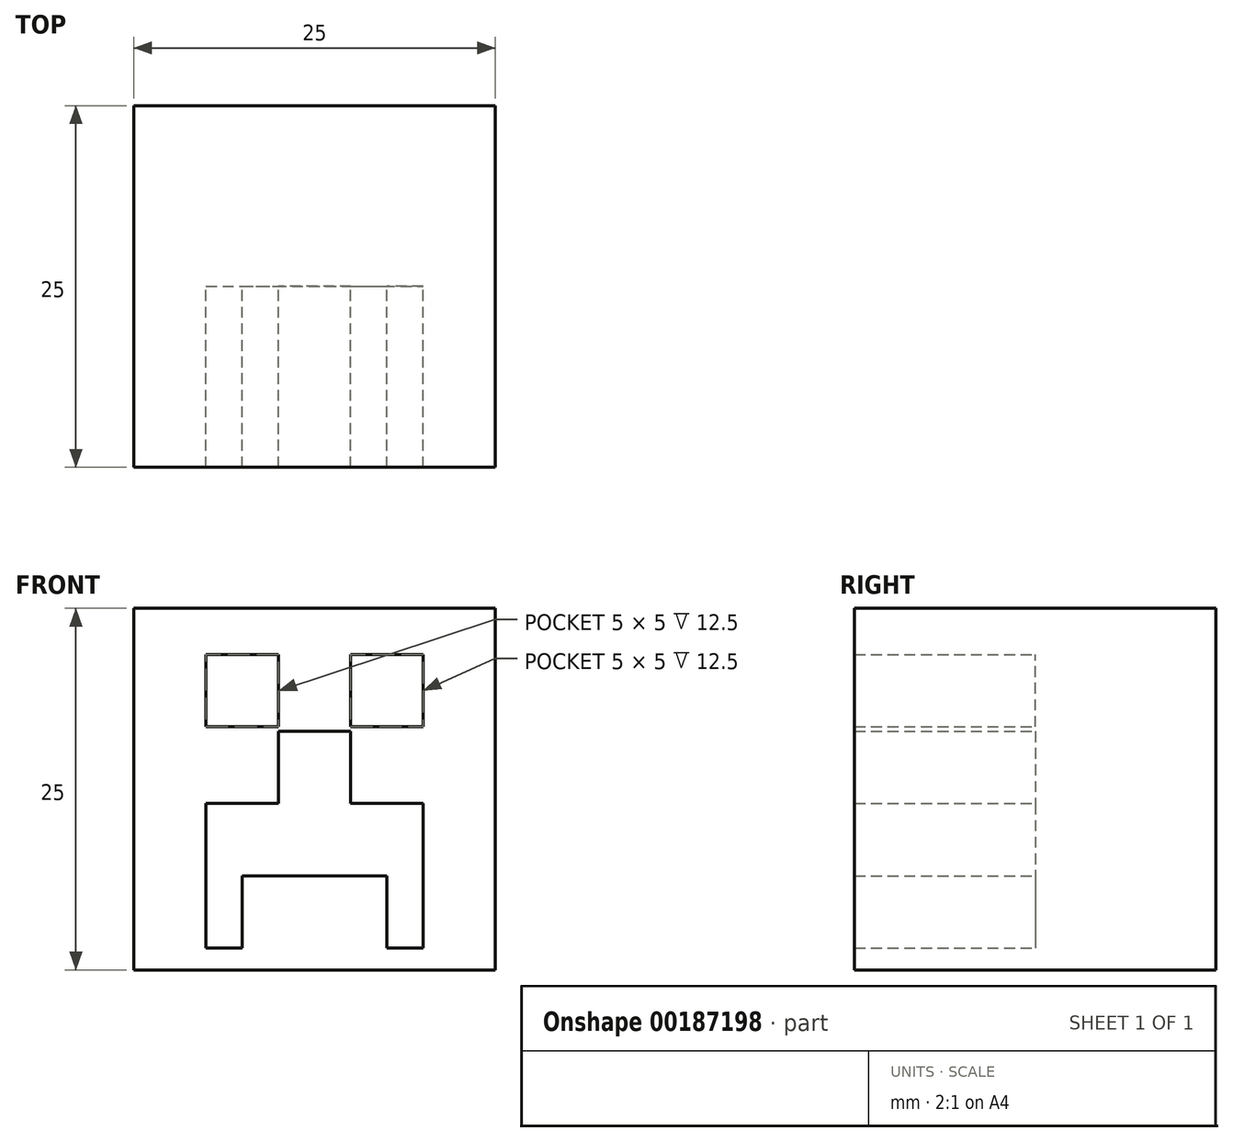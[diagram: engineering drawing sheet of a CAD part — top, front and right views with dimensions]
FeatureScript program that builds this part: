
annotation { "Feature Type Name" : "Feature", "Feature Type Description" : "" }
export const myFeature = defineFeature(function(context is Context, id is Id, definition is map)
    precondition{}
    {
        {
            var Q0;
            Q0=qCreatedBy(makeId("Front.planeOp"),FACE);
            var sketch = newSketch(context, id + "F0", { "sketchPlane" : qUnion([Q0])});
            skLineSegment(sketch, "E0.bottom", {"start": v(0, 0) * mm, "end": v(25, 0) * mm});
            skLineSegment(sketch, "E0.top", {"start": v(0, 25) * mm, "end": v(25, 25) * mm});
            skLineSegment(sketch, "E0.left", {"start": v(0, 0) * mm, "end": v(0, 25) * mm});
            skLineSegment(sketch, "E0.right", {"start": v(25, 0) * mm, "end": v(25, 25) * mm});
            skLineSegment(sketch, "E1.top", {"start": v(5, 21.8) * mm, "end": v(10, 21.8) * mm});
            skLineSegment(sketch, "E1.left", {"start": v(5, 16.8) * mm, "end": v(5, 21.8) * mm});
            skLineSegment(sketch, "E2.top", {"start": v(15, 21.8) * mm, "end": v(20, 21.8) * mm});
            skLineSegment(sketch, "E2.right", {"start": v(20, 16.8) * mm, "end": v(20, 21.8) * mm});
            skLineSegment(sketch, "E3.bottom", {"start": v(15, 16.5) * mm, "end": v(10, 16.5) * mm});
            skLineSegment(sketch, "E3.left", {"start": v(15, 16.5) * mm, "end": v(15, 11.5) * mm});
            skLineSegment(sketch, "E3.right", {"start": v(10, 16.5) * mm, "end": v(10, 11.5) * mm});
            skLineSegment(sketch, "E4.left", {"start": v(5, 11.5) * mm, "end": v(5, 6.5) * mm});
            skLineSegment(sketch, "E4.right", {"start": v(20, 11.5) * mm, "end": v(20, 6.5) * mm});
            skLineSegment(sketch, "E5.top", {"start": v(5, 1.5) * mm, "end": v(7.5, 1.5) * mm});
            skLineSegment(sketch, "E5.left", {"start": v(5, 6.5) * mm, "end": v(5, 1.5) * mm});
            skLineSegment(sketch, "E5.right", {"start": v(7.5, 6.5) * mm, "end": v(7.5, 1.5) * mm});
            skLineSegment(sketch, "E6.top", {"start": v(20, 1.5) * mm, "end": v(17.5, 1.5) * mm});
            skLineSegment(sketch, "E6.left", {"start": v(20, 6.5) * mm, "end": v(20, 1.5) * mm});
            skLineSegment(sketch, "E6.right", {"start": v(17.5, 6.5) * mm, "end": v(17.5, 1.5) * mm});
            skLineSegment(sketch, "E7", {"start": v(7.5, 6.5) * mm, "end": v(17.5, 6.5) * mm});
            skLineSegment(sketch, "E8", {"start": v(5, 11.5) * mm, "end": v(10, 11.5) * mm});
            skLineSegment(sketch, "E9", {"start": v(15, 11.5) * mm, "end": v(20, 11.5) * mm});
            skLineSegment(sketch, "E10", {"start": v(10, 21.8) * mm, "end": v(10, 16.8) * mm});
            skLineSegment(sketch, "E11", {"start": v(10, 16.8) * mm, "end": v(5, 16.8) * mm});
            skLineSegment(sketch, "E12", {"start": v(15, 21.8) * mm, "end": v(15, 16.8) * mm});
            skLineSegment(sketch, "E13", {"start": v(20, 16.8) * mm, "end": v(15, 16.8) * mm});
            skSolve(sketch);
        }
        {
            var Q0;
            Q0=makeQuery(id+"F0.imprint","IMPRINT",FACE,{"disambiguationData":[TD([[makeQuery(id+"F0.imprint","IMPRINT",EDGE,{"derivedFrom":sQuery(id+"F0.wireOp",EDGE,"E0.bottom")}),1.0]])]});
            extrude(context, id + "F1", {"entities" : qUnion([Q0]), "depth" : 12.5 * mm, "offsetDistance" : 25 * mm});
        }
        {
            var Q0;
            Q0=makeQuery(id+"F1.opExtrude","CAP_FACE",FACE,{"disambiguationData":[OSD([sQuery(id+"F0.wireOp",EDGE,"E0.bottom"),sQuery(id+"F0.wireOp",EDGE,"E0.top"),sQuery(id+"F0.wireOp",EDGE,"E0.left"),sQuery(id+"F0.wireOp",EDGE,"E0.right"),sQuery(id+"F0.wireOp",EDGE,"E1.bottom"),sQuery(id+"F0.wireOp",EDGE,"E1.top"),sQuery(id+"F0.wireOp",EDGE,"E1.left"),sQuery(id+"F0.wireOp",EDGE,"E1.right"),sQuery(id+"F0.wireOp",EDGE,"E2.bottom"),sQuery(id+"F0.wireOp",EDGE,"E2.top"),sQuery(id+"F0.wireOp",EDGE,"E2.left"),sQuery(id+"F0.wireOp",EDGE,"E2.right"),sQuery(id+"F0.wireOp",EDGE,"JrgWBdCO-lYkd-kNA1-mnFF-5CoDAToMzeUa"),sQuery(id+"F0.wireOp",EDGE,"U7jJjCgw-ri9h-lG7O-gbqt-uVueqERpd8xh"),sQuery(id+"F0.wireOp",EDGE,"uueTeX40-DStC-LOR1-AKgw-dmqD0makymWU"),sQuery(id+"F0.wireOp",EDGE,"krW0I0Pj-R1Rk-dPlv-WSJV-HO4J9WNeruJM"),sQuery(id+"F0.wireOp",EDGE,"riHXDhNq-QI2c-h9jh-RLNH-7ek7vr0C3tvY"),sQuery(id+"F0.wireOp",EDGE,"c9QX3juE-X68d-ZmeH-7pxM-RB1xVgo7sZpY"),sQuery(id+"F0.wireOp",EDGE,"ReVWC94K-ZfPy-mUbf-CNwC-PWcVKCl0MNJx"),sQuery(id+"F0.wireOp",EDGE,"GIeAFJTQ-raLs-h47B-s4HK-Tx1bOeoSCRzm")])],"isStart":true});
            var sketch = newSketch(context, id + "F2", { "sketchPlane" : qUnion([Q0])});
            skLineSegment(sketch, "E14.bottom", {"start": v(0, 0) * mm, "end": v(-25, 0) * mm});
            skLineSegment(sketch, "E14.top", {"start": v(0, 25) * mm, "end": v(-25, 25) * mm});
            skLineSegment(sketch, "E14.left", {"start": v(0, 0) * mm, "end": v(0, 25) * mm});
            skLineSegment(sketch, "E14.right", {"start": v(-25, 0) * mm, "end": v(-25, 25) * mm});
            skSolve(sketch);
        }
        {
            var Q0;
            Q0 = qSketchRegion(id + "F2", true);
            extrude(context, id + "F3", {"entities" : qUnion([Q0]), "operationType" : NewBodyOperationType.ADD, "depth" : 12.5 * mm, "offsetDistance" : 25 * mm});
        }
    });
